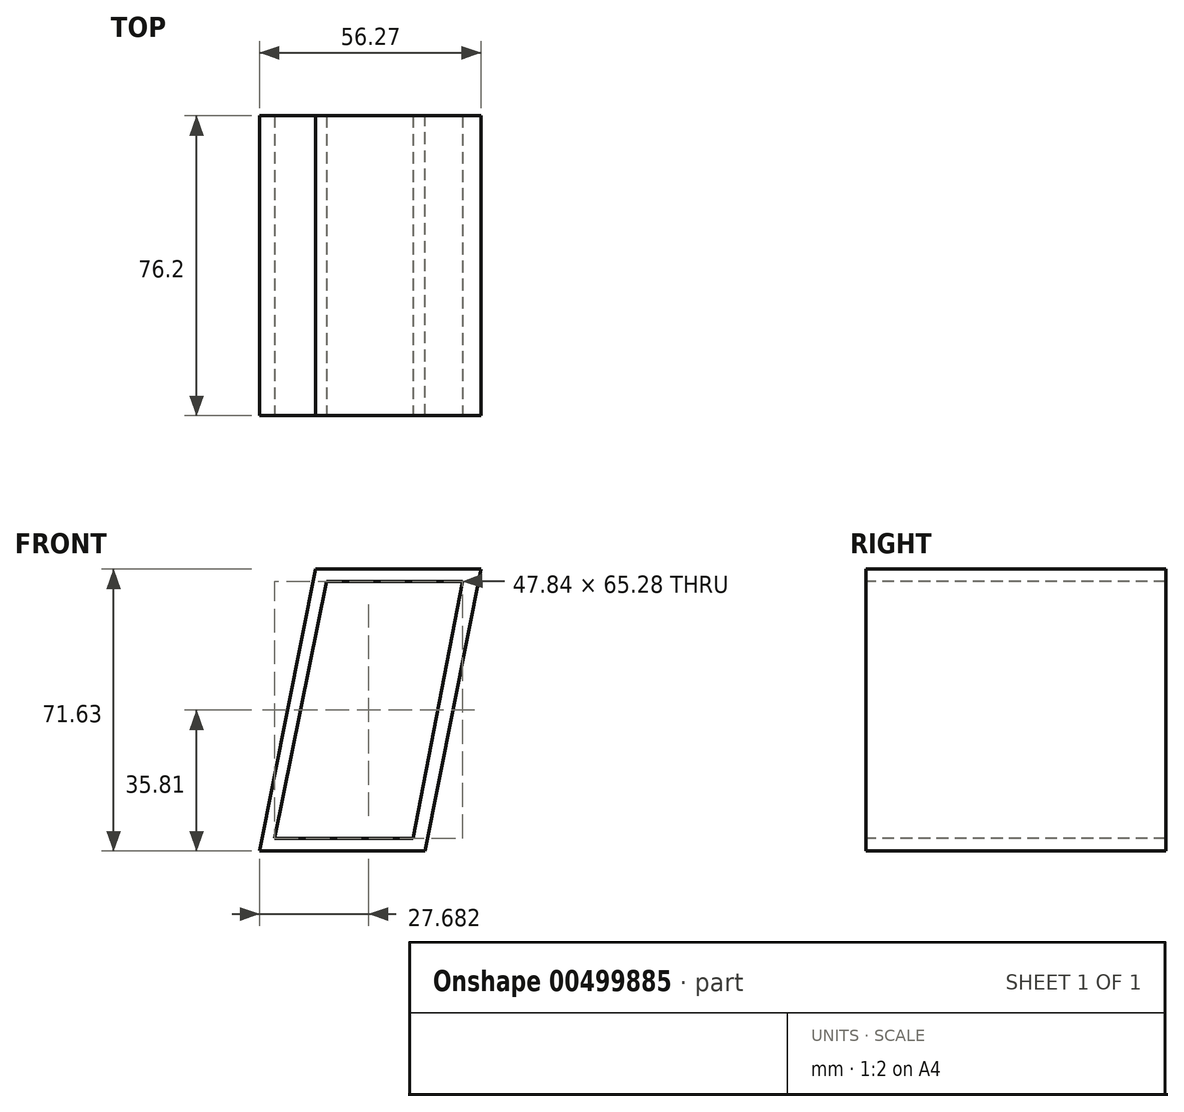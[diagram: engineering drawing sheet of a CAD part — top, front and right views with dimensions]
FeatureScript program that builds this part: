
annotation { "Feature Type Name" : "Feature", "Feature Type Description" : "" }
export const myFeature = defineFeature(function(context is Context, id is Id, definition is map)
    precondition{}
    {
        {
            var Q0;
            Q0=qCreatedBy(makeId("Front.planeOp"),FACE);
            var sketch = newSketch(context, id + "F0", { "sketchPlane" : qUnion([Q0])});
            skLineSegment(sketch, "E0", {"start": v(-57.72, 37.98) * mm, "end": v(-71.93, -33.65) * mm});
            skLineSegment(sketch, "E1", {"start": v(-71.93, -33.65) * mm, "end": v(-29.87, -33.65) * mm});
            skLineSegment(sketch, "E2", {"start": v(-29.87, -33.65) * mm, "end": v(-15.66, 37.98) * mm});
            skLineSegment(sketch, "E3", {"start": v(-15.66, 37.98) * mm, "end": v(-57.72, 37.98) * mm});
            skSolve(sketch);
        }
        {
            var Q0;
            Q0=makeQuery(id+"F0.imprint","IMPRINT",FACE,{"disambiguationData":[TD([[makeQuery(id+"F0.imprint","IMPRINT",EDGE,{"derivedFrom":sQuery(id+"F0.wireOp",EDGE,"E0")}),1.0]])]});
            extrude(context, id + "F1", {"entities" : qUnion([Q0]), "depth" : 76.2 * mm});
        }
        {
            var Q0;
            Q0=qCreatedBy(makeId("Front.planeOp"),FACE);
            var sketch = newSketch(context, id + "F2", { "sketchPlane" : qUnion([Q0])});
            skLineSegment(sketch, "E4", {"start": v(-20.33, 34.8) * mm, "end": v(-54.86, 34.8) * mm});
            skLineSegment(sketch, "E5", {"start": v(-32.97, -30.48) * mm, "end": v(-68.17, -30.48) * mm});
            skLineSegment(sketch, "E6", {"start": v(-68.17, -30.48) * mm, "end": v(-54.86, 34.8) * mm});
            skLineSegment(sketch, "E7", {"start": v(-20.33, 34.8) * mm, "end": v(-32.97, -30.48) * mm});
            skSolve(sketch);
        }
        {
            var Q0;
            Q0 = qSketchRegion(id + "F2", true);
            extrude(context, id + "F3", {"entities" : qUnion([Q0]), "operationType" : NewBodyOperationType.REMOVE, "endBound" : BoundingType.SYMMETRIC, "oppositeDirection" : true, "depth" : 203.2 * mm});
        }
    });
